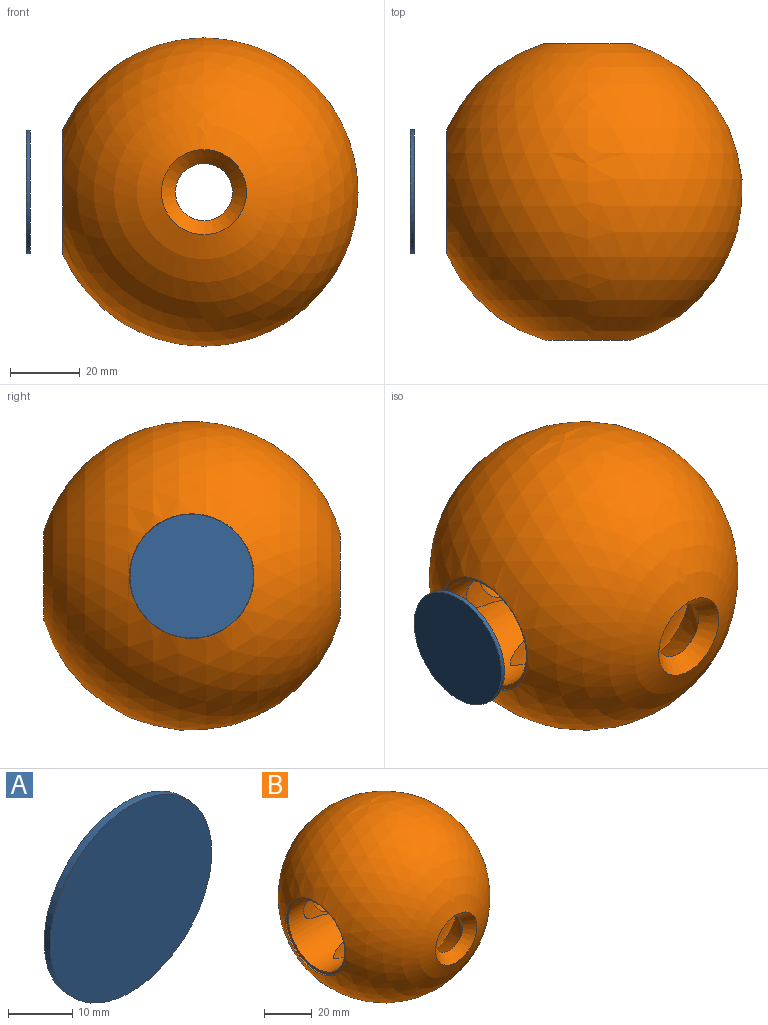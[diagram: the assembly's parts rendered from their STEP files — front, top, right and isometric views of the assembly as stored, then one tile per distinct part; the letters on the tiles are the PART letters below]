
ASSEMBLY  parts=2 mates=1
PART A: 3 faces, bbox 35.6x1.3x35.6 mm
  f0: cylinder r=17.78mm len=35.56mm, axis (0,-1,0), area 141.9mm2, adj f1,f2
  f1: plane 35.56x35.56mm, normal (0,1,0), area 993.1mm2, adj f0
  f2: plane 35.56x35.56mm, normal (0,-1,0), area 993.1mm2, adj f0
PART B: 10 faces, bbox 88.9x85.3x88.9 mm
  f0: sphere r=44.45mm, area 22778.7mm2, adj f3,f4,f8
  f1: revolved ~68x68mm, area 12516.7mm2, adj f2,f6,f7
  f2: revolved ~68x68mm, area 12516.7mm2, adj f1,f5,f7
  f3: cone r=6.35mm half-angle=22.5deg, axis (0,1,0), area 376.4mm2, adj f0,f6
  f4: cone r=12.23mm half-angle=43.5deg, axis (0,-1,0), area 374.7mm2, adj f0,f5
  f5: cone r=18.26mm half-angle=37.1deg, axis (0,1,0), area 1384.8mm2, adj f2,f4
  f6: cone r=10.74mm half-angle=30.7deg, axis (0,-1,0), area 1340.9mm2, adj f1,f3
  f7: cylinder r=16.65mm len=37.28mm, axis (-1,0,0), area 2327.7mm2, adj f1,f2,f9
  f8: cylinder r=17.92mm len=35.83mm, axis (-1,0,0), area 82.6mm2, adj f0,f9
  f9: plane 35.83x35.83mm, normal (-1,0,0), area 137.9mm2, adj f7,f8
PLACE A rot(axis=(0.58,-0.58,0.58),120deg) t=(-62.74,26.68,-8.37)mm
PLACE B t=(-12.8,26.68,-8.37)mm
MATE slider A.f0 <-> B.f7  axis (-1,0,0) through (-64.01,26.68,-8.37)mm
